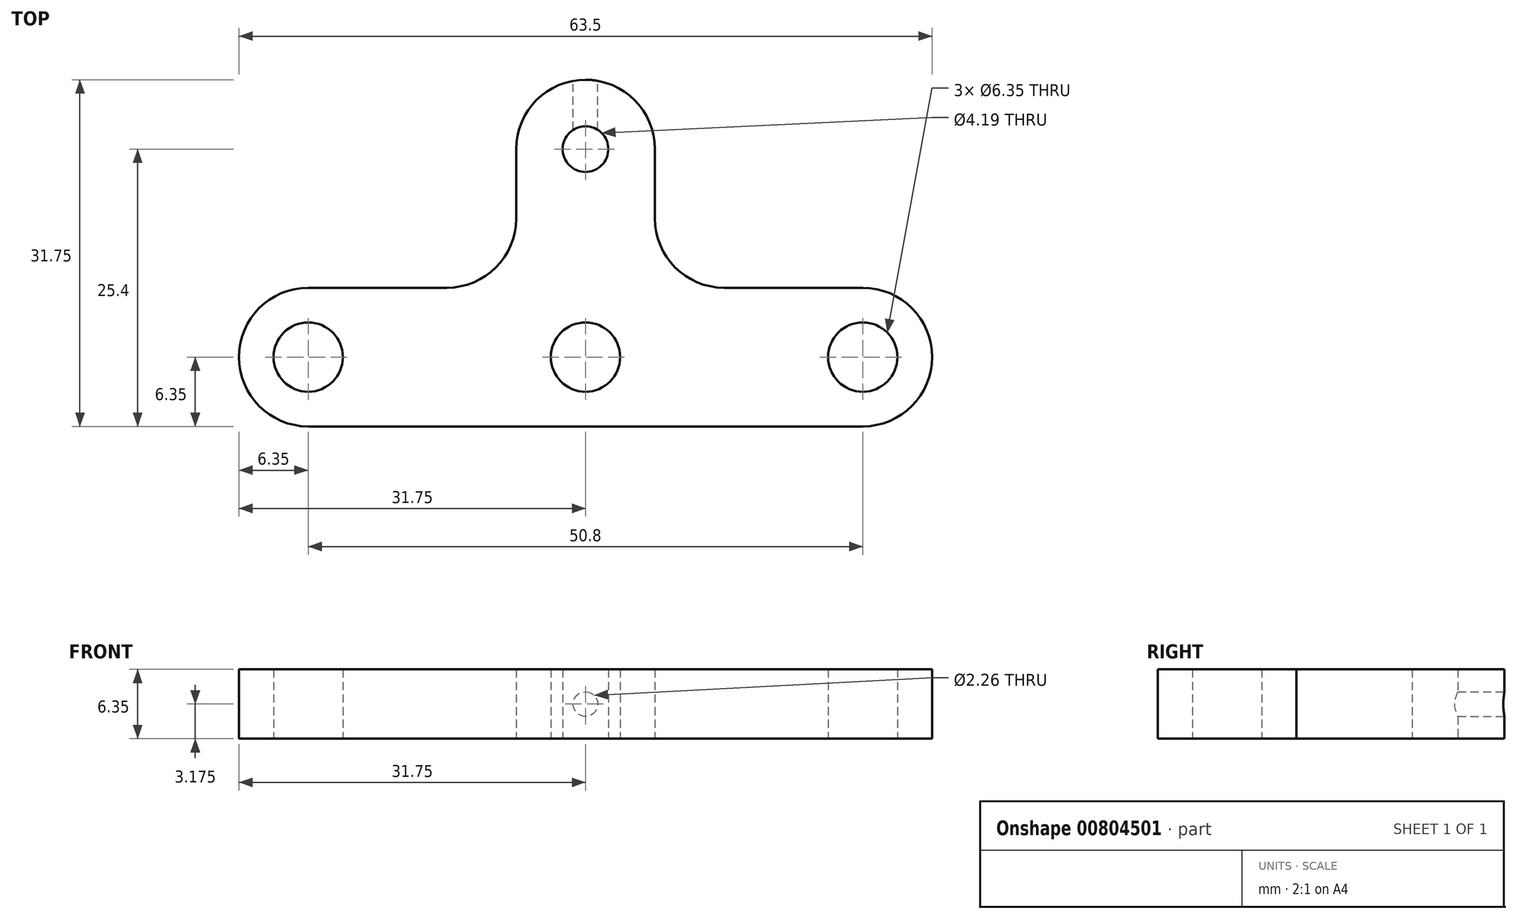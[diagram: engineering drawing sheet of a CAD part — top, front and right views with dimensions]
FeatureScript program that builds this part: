
annotation { "Feature Type Name" : "Feature", "Feature Type Description" : "" }
export const myFeature = defineFeature(function(context is Context, id is Id, definition is map)
    precondition{}
    {
        {
            var Q0;
            Q0=qCreatedBy(makeId("Top.planeOp"),FACE);
            var sketch = newSketch(context, id + "F0", { "sketchPlane" : qUnion([Q0])});
            skCircle(sketch, "E0", {"center": v(-25.4, 0) * mm, "radius": 6.35 * mm});
            skCircle(sketch, "E1", {"center": v(25.4, 0) * mm, "radius": 6.35 * mm});
            skLineSegment(sketch, "E2", {"start": v(-25.4, 0) * mm, "end": v(25.4, 0) * mm, "construction": true});
            skLineSegment(sketch, "E3", {"start": v(-25.4, -6.35) * mm, "end": v(25.4, -6.35) * mm});
            skCircle(sketch, "E4", {"center": v(0, 19.05) * mm, "radius": 6.35 * mm});
            skLineSegment(sketch, "E5", {"start": v(-6.35, 19.05) * mm, "end": v(-6.35, 12.7) * mm});
            skLineSegment(sketch, "E6", {"start": v(-12.7, 6.35) * mm, "end": v(-25.4, 6.35) * mm});
            skLineSegment(sketch, "E7", {"start": v(6.35, 19.05) * mm, "end": v(6.35, 12.7) * mm});
            skLineSegment(sketch, "E8", {"start": v(12.7, 6.35) * mm, "end": v(25.4, 6.35) * mm});
            skPoint(sketch, "E9.visualSharp", {"position": v(-6.35, 6.35) * mm});
            skArc(sketch, "E9.filletArc", {"start": v(-12.7, 6.35) * mm, "mid": v(-8.2, 8.2) * mm, "end": v(-6.35, 12.7) * mm});
            skPoint(sketch, "E10.visualSharp", {"position": v(6.35, 6.35) * mm});
            skArc(sketch, "E10.filletArc", {"start": v(6.35, 12.7) * mm, "mid": v(8.2, 8.2) * mm, "end": v(12.7, 6.35) * mm});
            skCircle(sketch, "E11", {"center": v(0, 19.05) * mm, "radius": 2.1 * mm});
            skCircle(sketch, "E12", {"center": v(-25.4, 0) * mm, "radius": 3.18 * mm});
            skCircle(sketch, "E13", {"center": v(25.4, 0) * mm, "radius": 3.18 * mm});
            skCircle(sketch, "E14", {"center": v(0, 0) * mm, "radius": 3.18 * mm});
            skSolve(sketch);
        }
        {
            var Q0;
            Q0 = qSketchRegion(id + "F0", true);
            extrude(context, id + "F1", {"entities" : qUnion([Q0]), "depth" : 6.35 * mm, "offsetDistance" : 25.4 * mm});
        }
        {
            var Q0;
            Q0=makeQuery(id+"F1.opExtrude","CAP_EDGE",EDGE,{"disambiguationData":[OSD([sQuery(id+"F0.wireOp",EDGE,"E4")])],"isStart":true});
            cPoint(context, id + "F2", {"entities" : qUnion([Q0]), "parameter" : 0.5});
        }
        {
            var Q0;
            Q0=qCreatedBy(makeId("Front.planeOp"),FACE);
            var Q1;
            Q1 = qCreatedBy(id + "F2" ,VERTEX);
            cPlane(context, id + "F3", {"entities" : qUnion([Q0, Q1]), "cplaneType" : CPlaneType.PLANE_POINT, "offset" : 25.4 * mm, "width" : 152.4 * mm, "height" : 152.4 * mm});
        }
        {
            var Q0;
            Q0=qCreatedBy(id+"F3.planeOp",FACE);
            var Q1;
            Q1=qCreatedBy(id+"F3.planeOp",FACE);
            var sketch = newSketch(context, id + "F4", { "sketchPlane" : qUnion([Q0, Q1])});
            skLineSegment(sketch, "E15.0.0", {"start": v(-6.35, 0) * mm, "end": v(6.35, 0) * mm, "construction": true});
            skLineSegment(sketch, "E15.0.1", {"start": v(-6.35, 0) * mm, "end": v(-6.35, 6.35) * mm, "construction": true});
            skLineSegment(sketch, "E15.0.2", {"start": v(6.35, 6.35) * mm, "end": v(-6.35, 6.35) * mm, "construction": true});
            skLineSegment(sketch, "E15.0.3", {"start": v(6.35, 6.35) * mm, "end": v(6.35, 0) * mm, "construction": true});
            skLineSegment(sketch, "E16", {"start": v(6.35, 6.35) * mm, "end": v(-6.35, 0) * mm, "construction": true});
            skPoint(sketch, "E17", {"position": v(0, 3.18) * mm});
            skSolve(sketch);
        }
        {
            var Q0;
            Q0=sQuery(id+"F4.wireOp",VERTEX,"E17");
            var Q1;
            Q1=makeQuery(id+"F1.opExtrude","SWEPT_BODY",BODY,{"disambiguationData":[OSD([sQuery(id+"F0.wireOp",EDGE,"E0"),sQuery(id+"F0.wireOp",EDGE,"E1"),sQuery(id+"F0.wireOp",EDGE,"E3"),sQuery(id+"F0.wireOp",EDGE,"E4"),sQuery(id+"F0.wireOp",EDGE,"E5"),sQuery(id+"F0.wireOp",EDGE,"E6"),sQuery(id+"F0.wireOp",EDGE,"E7"),sQuery(id+"F0.wireOp",EDGE,"E8"),sQuery(id+"F0.wireOp",EDGE,"E9.filletArc"),sQuery(id+"F0.wireOp",EDGE,"E10.filletArc"),sQuery(id+"F0.wireOp",EDGE,"E11"),sQuery(id+"F0.wireOp",EDGE,"E12"),sQuery(id+"F0.wireOp",EDGE,"E13"),sQuery(id+"F0.wireOp",EDGE,"E14")])]});
            hole(context, id + "F5", {"style" : HoleStyle.SIMPLE, "endStyle" : HoleEndStyle.BLIND, "oppositeDirection" : true, "standardTappedOrClearance" : lookupTablePath({ "standard" : "ANSI", "engagement" : "75%", "pitch" : "40 tpi", "size" : "#4", "type" : "Tapped" }), "standardBlindInLast" : lookupTablePath({ "standard" : "ANSI", "fit" : "Normal", "engagement" : "75%", "pitch" : "40 tpi", "size" : "#4", "type" : "Clearance & tapped" }), "holeDiameter" : 2.26 * mm, "majorDiameter" : 2.84 * mm, "showTappedDepth" : true, "holeDepth" : 5.08 * mm, "isTappedThrough" : true, "tappedDepth" : 5.08 * mm, "tapClearance" : 0, "locations" : qUnion([Q0]), "scope" : qUnion([Q1])});
        }
    });
